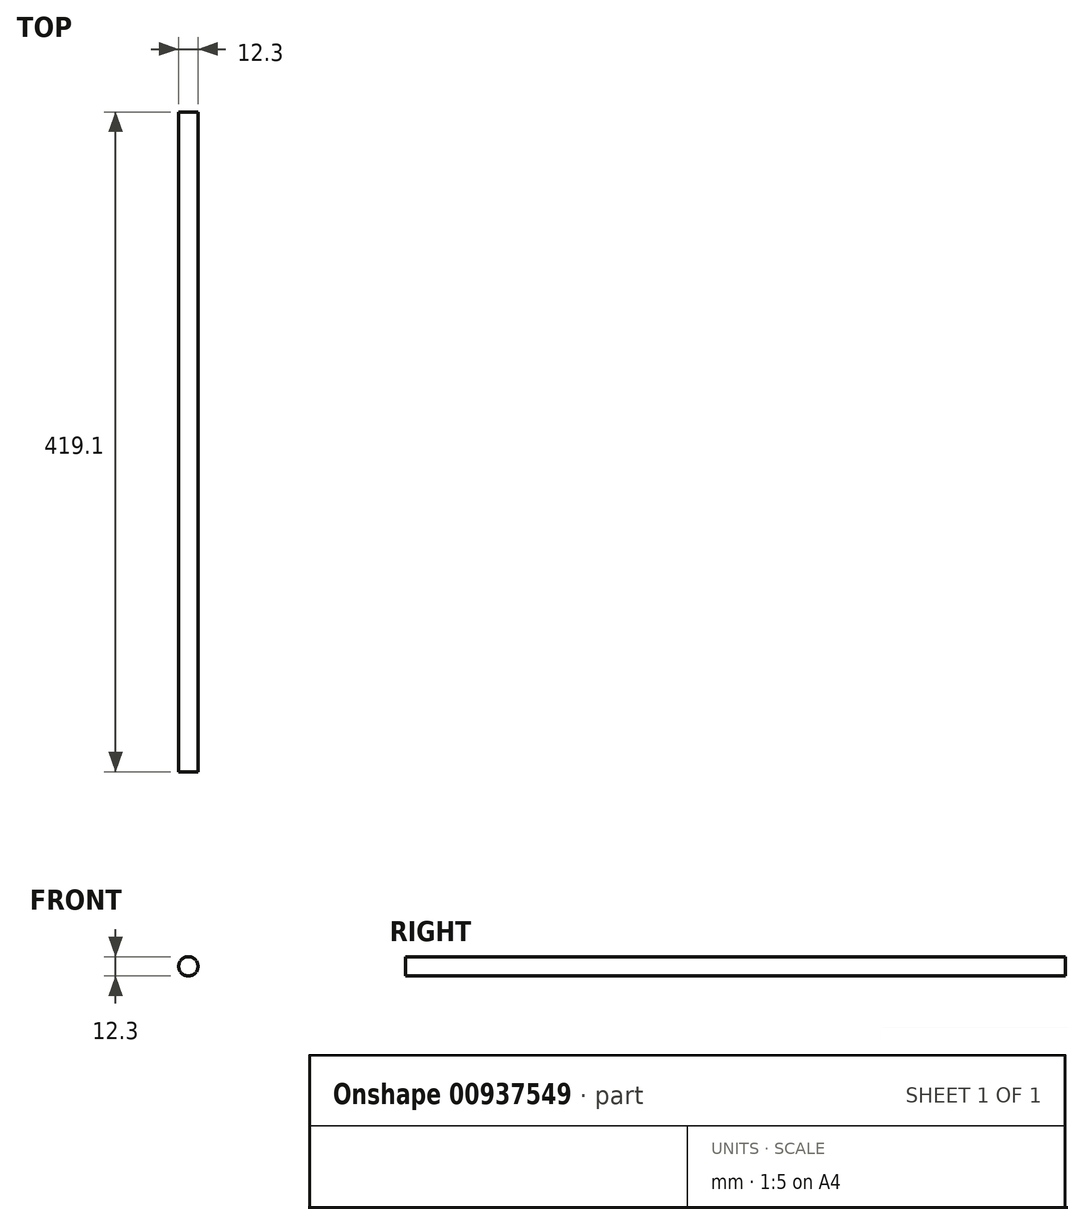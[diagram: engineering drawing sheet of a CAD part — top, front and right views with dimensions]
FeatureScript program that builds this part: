
annotation { "Feature Type Name" : "Feature", "Feature Type Description" : "" }
export const myFeature = defineFeature(function(context is Context, id is Id, definition is map)
    precondition{}
    {
        {
            var Q0;
            Q0=qCreatedBy(makeId("Front.planeOp"),FACE);
            var sketch = newSketch(context, id + "F0", { "sketchPlane" : qUnion([Q0])});
            skCircle(sketch, "E0", {"center": v(0, 0) * mm, "radius": 6.15 * mm});
            skSolve(sketch);
        }
        {
            var Q0;
            Q0=qSketchRegion(id+"F0",true);
            extrude(context, id + "F1", {"entities" : qUnion([Q0]), "depth" : 419.1 * mm, "offsetDistance" : 25.4 * mm});
        }
    });
